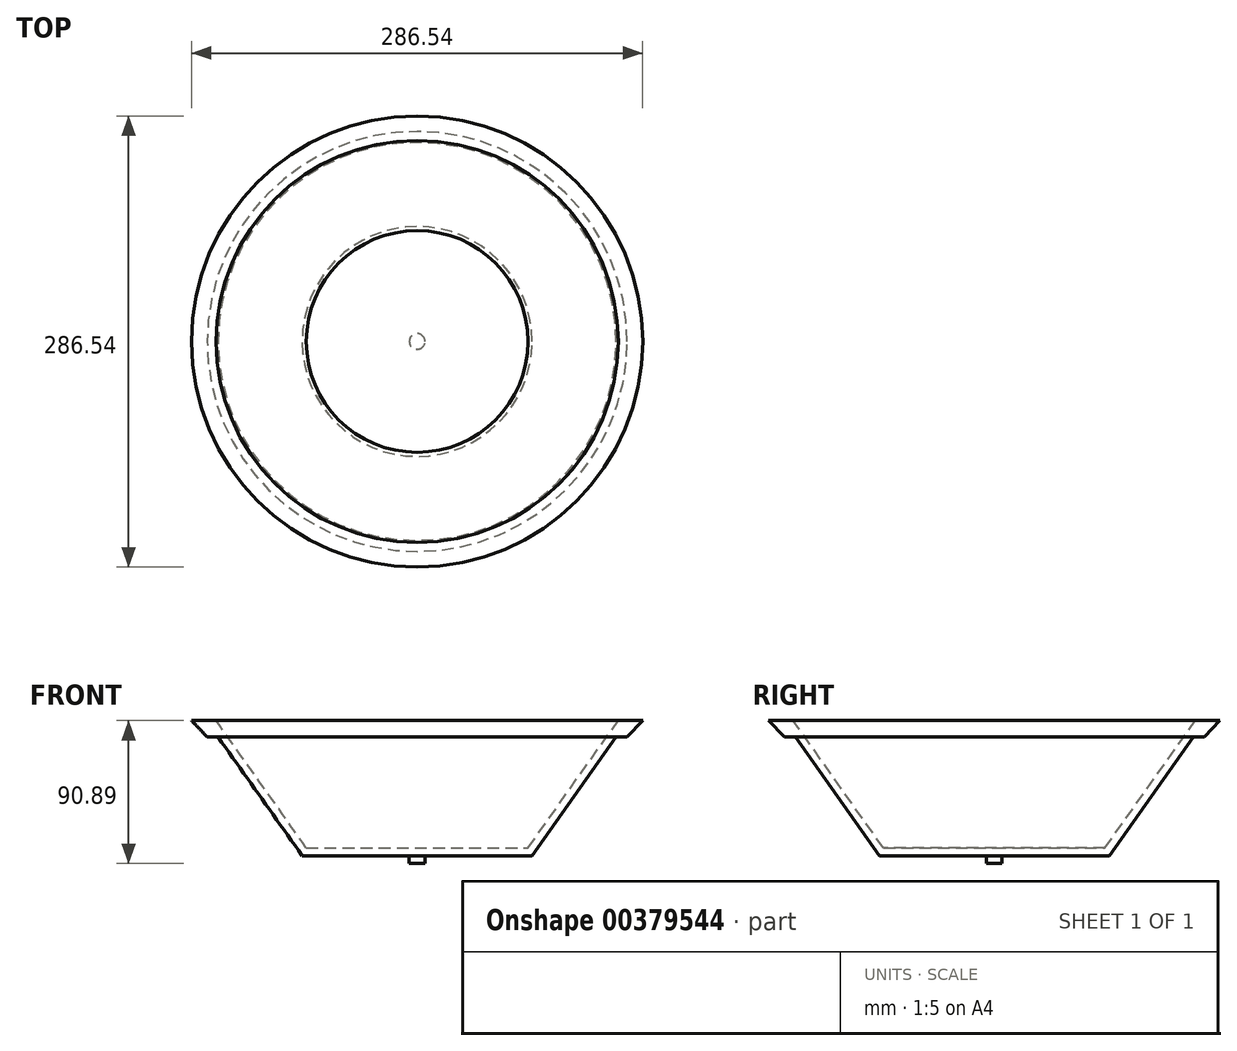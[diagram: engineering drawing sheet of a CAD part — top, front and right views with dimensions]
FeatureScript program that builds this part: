
annotation { "Feature Type Name" : "Feature", "Feature Type Description" : "" }
export const myFeature = defineFeature(function(context is Context, id is Id, definition is map)
    precondition{}
    {
        {
            var Q0;
            Q0=qCreatedBy(makeId("Front.planeOp"),FACE);
            var sketch = newSketch(context, id + "F0", { "sketchPlane" : qUnion([Q0])});
            skLineSegment(sketch, "E0", {"start": v(0, 0) * mm, "end": v(0, 383.65) * mm, "construction": true});
            skLineSegment(sketch, "E1", {"start": v(0, 0) * mm, "end": v(-73, 0) * mm});
            skLineSegment(sketch, "E2", {"start": v(-73, 0) * mm, "end": v(-126.37, 75.32) * mm});
            skLineSegment(sketch, "E3", {"start": v(-126.37, 75.32) * mm, "end": v(-133.33, 75.32) * mm});
            skLineSegment(sketch, "E4", {"start": v(-133.33, 75.32) * mm, "end": v(-143.27, 85.9) * mm});
            skLineSegment(sketch, "E5", {"start": v(-143.27, 85.9) * mm, "end": v(-127.73, 85.9) * mm});
            skLineSegment(sketch, "E6.0", {"start": v(-70.41, 5) * mm, "end": v(-127.73, 85.9) * mm});
            skLineSegment(sketch, "E7.0", {"start": v(0, 5) * mm, "end": v(-70.41, 5) * mm});
            skLineSegment(sketch, "E8", {"start": v(0, 5) * mm, "end": v(0, 0) * mm});
            skLineSegment(sketch, "E9", {"start": v(0, 0) * mm, "end": v(0, -5) * mm});
            skLineSegment(sketch, "E10", {"start": v(0, -5) * mm, "end": v(-5, -5) * mm});
            skLineSegment(sketch, "E11", {"start": v(-5, -5) * mm, "end": v(-5, 0) * mm});
            skSolve(sketch);
        }
        {
            var Q0;
            Q0=makeQuery(id+"F0.imprint","IMPRINT",FACE,{"disambiguationData":[TD([[makeQuery(id+"F0.imprint","IMPRINT",EDGE,{"derivedFrom":sQuery(id+"F0.wireOp",EDGE,"E1")}),-1.0]])]});
            var Q1;
            {var subQ0=sQuery(id+"F0.wireOp",EDGE,"E9");Q1=makeQuery(id+"F0.imprint","IMPRINT",FACE,{"disambiguationData":[TD([[makeQuery(id+"F0.imprint","IMPRINT",EDGE,{"derivedFrom":subQ0}),-1.0]])]});}
            var Q2;
            Q2=sQuery(id+"F0.wireOp",EDGE,"E0");
            revolve(context, id + "F1", {"entities" : qUnion([Q0, Q1]), "axis" : qUnion([Q2]), "revolveType" : RevolveType.FULL});
        }
    });
